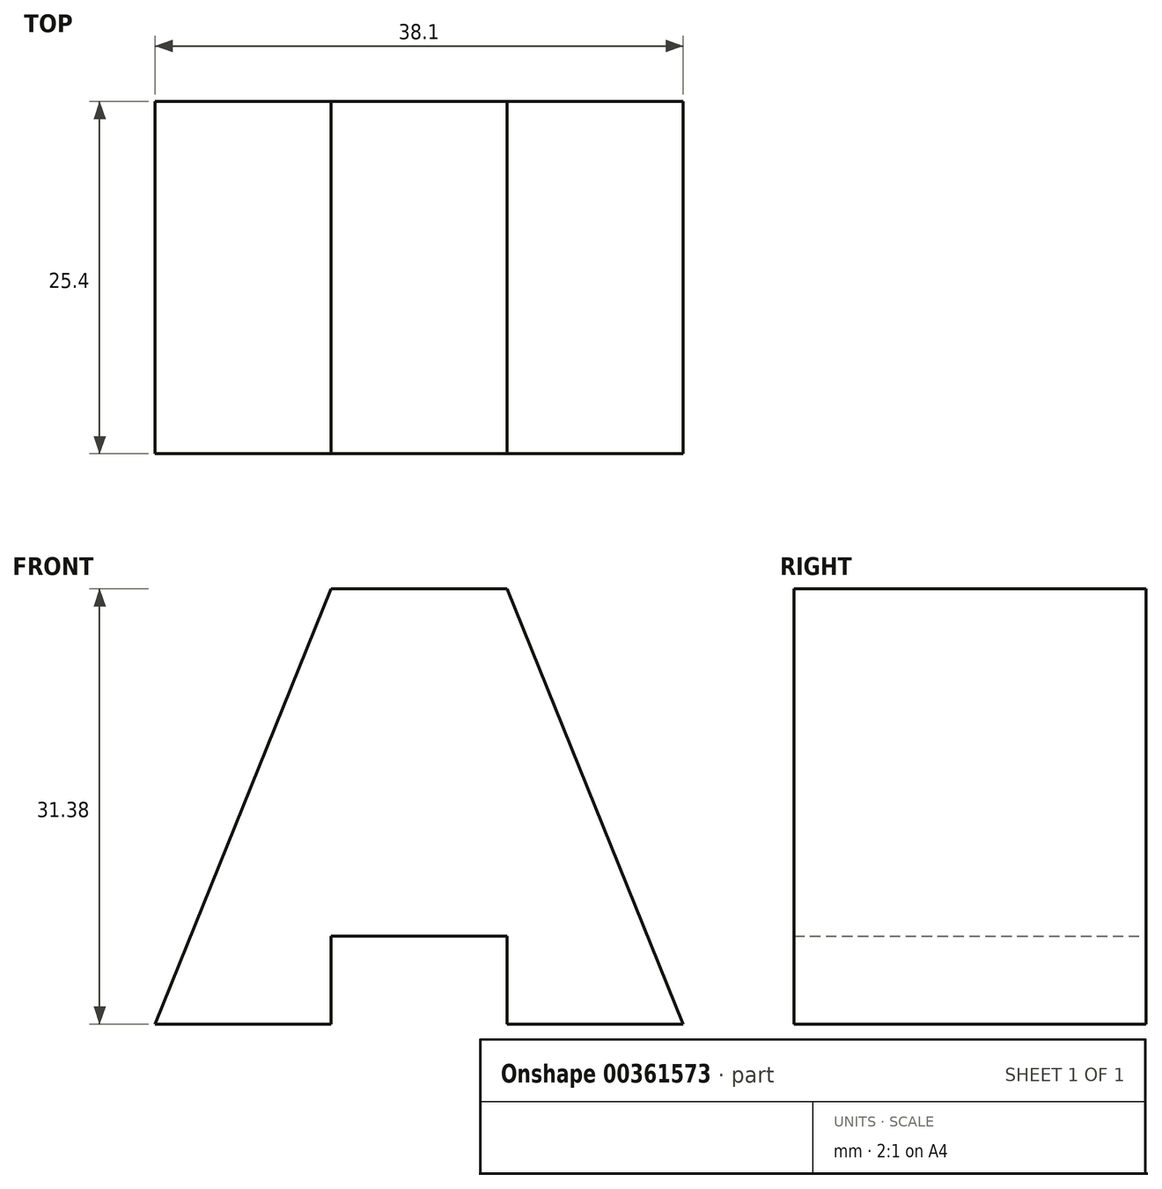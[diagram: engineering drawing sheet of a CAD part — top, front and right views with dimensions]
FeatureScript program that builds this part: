
annotation { "Feature Type Name" : "Feature", "Feature Type Description" : "" }
export const myFeature = defineFeature(function(context is Context, id is Id, definition is map)
    precondition{}
    {
        {
            var Q0;
            Q0=qCreatedBy(makeId("Front.planeOp"),FACE);
            var sketch = newSketch(context, id + "F0", { "sketchPlane" : qUnion([Q0])});
            skLineSegment(sketch, "E0", {"start": v(0, 0) * mm, "end": v(12.7, 31.38) * mm});
            skLineSegment(sketch, "E1", {"start": v(12.7, 31.38) * mm, "end": v(25.4, 31.38) * mm});
            skLineSegment(sketch, "E2", {"start": v(25.4, 31.38) * mm, "end": v(38.1, 0) * mm});
            skLineSegment(sketch, "E3", {"start": v(38.1, 0) * mm, "end": v(25.4, 0) * mm});
            skLineSegment(sketch, "E4", {"start": v(25.4, 0) * mm, "end": v(25.4, 6.35) * mm});
            skLineSegment(sketch, "E5", {"start": v(25.4, 6.35) * mm, "end": v(12.7, 6.35) * mm});
            skLineSegment(sketch, "E6", {"start": v(12.7, 6.35) * mm, "end": v(12.7, 0) * mm});
            skLineSegment(sketch, "E7", {"start": v(12.7, 0) * mm, "end": v(0, 0) * mm});
            skSolve(sketch);
        }
        {
            var Q0;
            Q0=makeQuery(id+"F0.imprint","IMPRINT",FACE,{"disambiguationData":[TD([[makeQuery(id+"F0.imprint","IMPRINT",EDGE,{"derivedFrom":sQuery(id+"F0.wireOp",EDGE,"E0")}),-1.0]])]});
            extrude(context, id + "F1", {"entities" : qUnion([Q0]), "depth" : 25.4 * mm});
        }
    });
